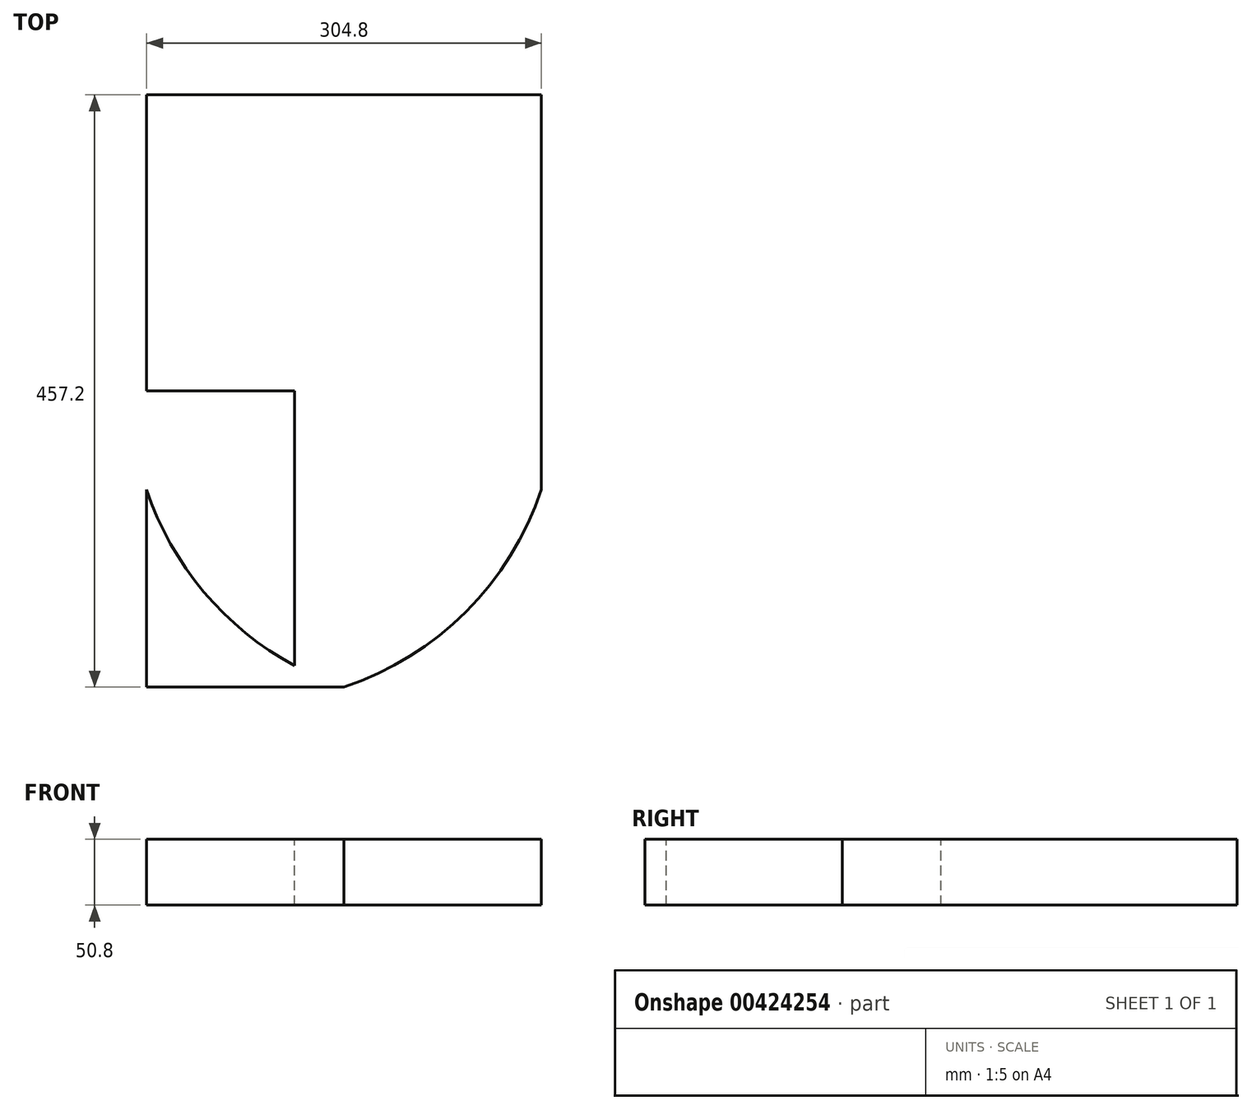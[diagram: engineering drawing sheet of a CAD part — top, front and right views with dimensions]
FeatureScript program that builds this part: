
annotation { "Feature Type Name" : "Feature", "Feature Type Description" : "" }
export const myFeature = defineFeature(function(context is Context, id is Id, definition is map)
    precondition{}
    {
        {
            var Q0;
            Q0=qCreatedBy(makeId("Top.planeOp"),FACE);
            var sketch = newSketch(context, id + "F0", { "sketchPlane" : qUnion([Q0])});
            skLineSegment(sketch, "E0.bottom", {"start": v(-152.4, -228.6) * mm, "end": v(152.4, -228.6) * mm});
            skLineSegment(sketch, "E0.top", {"start": v(-152.4, 228.6) * mm, "end": v(152.4, 228.6) * mm});
            skLineSegment(sketch, "E0.left", {"start": v(-152.4, -228.6) * mm, "end": v(-152.4, 228.6) * mm});
            skLineSegment(sketch, "E0.right", {"start": v(152.4, -228.6) * mm, "end": v(152.4, 228.6) * mm});
            skPoint(sketch, "E0.middle", {"position": v(0, 0) * mm});
            skSolve(sketch);
        }
        {
            var Q0;
            Q0=makeQuery(id+"F0.imprint","IMPRINT",FACE,{"disambiguationData":[TD([[makeQuery(id+"F0.imprint","IMPRINT",EDGE,{"derivedFrom":sQuery(id+"F0.wireOp",EDGE,"E0.bottom")}),1.0]])]});
            extrude(context, id + "F1", {"entities" : qUnion([Q0]), "depth" : 50.8 * mm});
        }
        {
            var Q0;
            Q0=makeQuery(id+"F1.opExtrude","CAP_FACE",FACE,{"disambiguationData":[OSD([sQuery(id+"F0.wireOp",EDGE,"E0.bottom"),sQuery(id+"F0.wireOp",EDGE,"E0.top"),sQuery(id+"F0.wireOp",EDGE,"E0.left"),sQuery(id+"F0.wireOp",EDGE,"E0.right")])],"isStart":false});
            var sketch = newSketch(context, id + "F2", { "sketchPlane" : qUnion([Q0])});
            skLineSegment(sketch, "E1", {"start": v(0, 0) * mm, "end": v(76.2, 0) * mm});
            skLineSegment(sketch, "E2", {"start": v(0, 0) * mm, "end": v(-76.2, 0) * mm});
            skLineSegment(sketch, "E3", {"start": v(-76.2, 0) * mm, "end": v(-152.4, 0) * mm});
            skLineSegment(sketch, "E4", {"start": v(76.2, 0) * mm, "end": v(152.4, 0) * mm});
            skArc(sketch, "E5", {"start": v(0, -228.6) * mm, "mid": v(94.19, -170.39) * mm, "end": v(152.4, -76.2) * mm});
            skArc(sketch, "E6", {"start": v(0, -228.6) * mm, "mid": v(-94.19, -170.39) * mm, "end": v(-152.4, -76.2) * mm});
            skLineSegment(sketch, "E7", {"start": v(-152.4, 77.45) * mm, "end": v(152.4, 77.45) * mm});
            skLineSegment(sketch, "E8.bottom", {"start": v(-38.1, 228.6) * mm, "end": v(38.1, 228.6) * mm});
            skLineSegment(sketch, "E8.top", {"start": v(-38.1, -228.6) * mm, "end": v(38.1, -228.6) * mm});
            skLineSegment(sketch, "E8.left", {"start": v(-38.1, 228.6) * mm, "end": v(-38.1, -228.6) * mm});
            skLineSegment(sketch, "E8.right", {"start": v(38.1, 228.6) * mm, "end": v(38.1, -228.6) * mm});
            skPoint(sketch, "E8.middle", {"position": v(0, 0) * mm});
            skLineSegment(sketch, "E9", {"start": v(152.4, 153.34) * mm, "end": v(-152.4, 153.34) * mm});
            skSolve(sketch);
        }
        {
            var Q0;
            Q0 = qSketchRegion(id + "F2", true);
            var Q1;
            Q1=makeQuery(id+"F2.imprint","IMPRINT",FACE,{"disambiguationData":[TD([[makeQuery(id+"F2.imprint","IMPRINT",EDGE,{"derivedFrom":sQuery(id+"F2.wireOp",EDGE,"E1")}),-1.0]])]});
            extrude(context, id + "F3", {"entities" : qUnion([Q0, Q1]), "operationType" : NewBodyOperationType.ADD, "oppositeDirection" : true, "depth" : 50.8 * mm});
        }
        {
            var Q0;
            {var subQ0=sQuery(id+"F2.wireOp",EDGE,"E6");Q0=makeQuery(id+"F2.imprint","IMPRINT",FACE,{"disambiguationData":[TD([[makeQuery(id+"F2.imprint","IMPRINT",EDGE,{"derivedFrom":subQ0}),1.0]])]});}
            extrude(context, id + "F4", {"entities" : qUnion([Q0]), "operationType" : NewBodyOperationType.REMOVE, "oppositeDirection" : true, "depth" : 50.8 * mm});
        }
        {
            var Q0;
            {var subQ0=sQuery(id+"F2.wireOp",EDGE,"E5");Q0=makeQuery(id+"F2.imprint","IMPRINT",FACE,{"disambiguationData":[TD([[makeQuery(id+"F2.imprint","IMPRINT",EDGE,{"derivedFrom":subQ0}),-1.0]])]});}
            extrude(context, id + "F5", {"entities" : qUnion([Q0]), "operationType" : NewBodyOperationType.REMOVE, "oppositeDirection" : true, "depth" : 50.8 * mm});
        }
        {
            var Q0;
            {var subQ0=sQuery(id+"F2.wireOp",EDGE,"E6");var subQ1=makeQuery(id+"F1.opExtrude","CAP_EDGE",EDGE,{"disambiguationData":[OSD([sQuery(id+"F0.wireOp",EDGE,"E0.left")])],"isStart":false});var subQ2=makeQuery(id+"F2.imprint","INTERSECT",VERTEX,{"derivedFrom":[subQ1,subQ0]});Q0=makeQuery(id+"F2.imprint","IMPRINT",FACE,{"disambiguationData":[TD([[makeQuery(id+"F2.imprint","IMPRINT",EDGE,{"disambiguationData":[TD([[subQ2,1.0]])],"derivedFrom":subQ0}),1.0]])]});}
            var Q1;
            {var subQ0=sQuery(id+"F2.wireOp",EDGE,"E5");var subQ1=makeQuery(id+"F1.opExtrude","CAP_EDGE",EDGE,{"disambiguationData":[OSD([sQuery(id+"F0.wireOp",EDGE,"E0.right")])],"isStart":false});var subQ2=makeQuery(id+"F2.imprint","INTERSECT",VERTEX,{"derivedFrom":[subQ1,subQ0]});Q1=makeQuery(id+"F2.imprint","IMPRINT",FACE,{"disambiguationData":[TD([[makeQuery(id+"F2.imprint","IMPRINT",EDGE,{"disambiguationData":[TD([[subQ2,1.0]])],"derivedFrom":subQ0}),-1.0]])]});}
            extrude(context, id + "F6", {"entities" : qUnion([Q0, Q1]), "operationType" : NewBodyOperationType.REMOVE, "oppositeDirection" : true, "depth" : 50.8 * mm});
        }
    });
